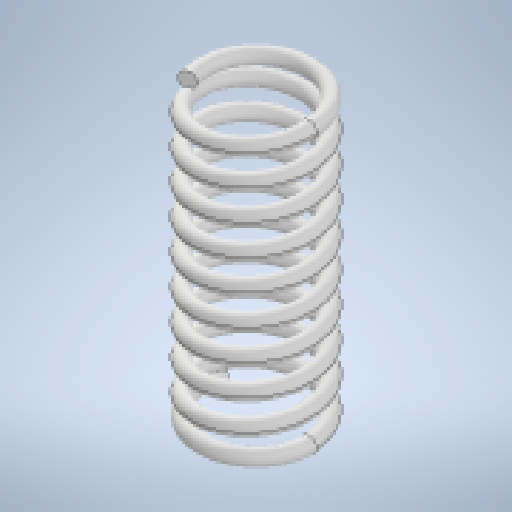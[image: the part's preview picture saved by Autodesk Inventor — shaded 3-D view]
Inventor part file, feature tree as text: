
AUTODESK INVENTOR PART (.ipt)
format: ipt  version: 2023 (Build 270158000, 158)  size: 395,264 bytes
history: native  units: mm
features: sketch x3, revolve x2, helix x1
ambient origin geometry x8: Origin, YZ Plane, XZ Plane, XY Plane, X Axis, Y Axis, Z Axis, Center Point
bodies: Solid1 (feature_tree)
feature tree (6):
  helix  "Coil1"  [1 undecoded]
  revolve  "Revolution1"  [1 undecoded]
  revolve  "Revolution2"  [1 undecoded]
  sketch  "Sketch1"  dims[d1=3.5mm]
  sketch  "Sketch2"  dims[d2=2.0mm d3=10.0mm d4=90.0mm d5=0.0mm d6=90.0deg d7=90.0deg d8=0.0mm d9=0.0mm d10=3.5mm]
  sketch  "Sketch3"  dims[d11=34.906585mm d12=3.5mm d13=34.906585mm]
note: 3 required parameter values undecoded (feature->parameter linkage not recoverable at this tier; creation-order binding heuristic only, values carry confidence <= 0.55)